# Revit family: FantiniCosmi_BIM_C48
name_source: partatom
category: Modelli generici
units: mm (PartAtom-declared; Revit-internal decimal feet)

## family parameters
Basato su piano di lavoro = No
Condiviso = No
Punto di calcolo locali = No
Può ospitare armatura = No
Quota connettore circolare = Usa diametro
Sempre verticale = Sì
Taglio con vuoti quando caricato = No
Tipo di parte = Normale

## types (1)
- Standard
    Body admissible temperature = - 10 ÷ 50 °C
    COLOR = Anthracite
    Catalog web link = https://www.fantinicosmi.it
    Descrizione = Flush-mounting room thermostat, with batteries, 1 temperature level
    Differential = ± 0,5 K
    POWER SUPPLY = 3 batteries AAA 1,5 V
    Part Number = Therm C48
    Prospetto di default = 0 mm  [stored 0 ft]
    Protection Degree = IP20
    Temperature regulation range = 5 ÷ 30 °C
    Unit weight = 0,13 Kg

note: [stored X ft] marks values corroborated as IEEE doubles in the binary element streams (Revit-internal decimal feet)

## geometry (parser evidence)
native form markers: Sweep x3
no freeform markers — native parametric forms only
